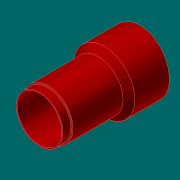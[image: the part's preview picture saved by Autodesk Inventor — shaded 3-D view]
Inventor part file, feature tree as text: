
AUTODESK INVENTOR PART (.ipt)
format: ipt  version: 2017.3 (Build 213256000, 256)  size: 176,128 bytes
history: native  units: in
note: dims shown in document units (in); Inventor stores cm internally (conversion verified against a paired STEP export)
features: extrude x4, sketch x3, chamfer x1, fillet x1
ambient origin geometry x8: Origin, YZ Plane, XZ Plane, XY Plane, X Axis, Y Axis, Z Axis, Center Point
bodies: Solid1 (feature_tree)
feature tree (9):
  sketch  "Sketch1"  dims[d0=2.875in d1=2.5984in]
  extrude  "Extrusion1"  Depth=2.5984in
  extrude  "Extrusion4"  Depth=21.25in
  chamfer  "Chamfer1"  Distance=0.5in
  extrude  "Extrusion2"  Depth=0.0312in TaperAngle=0.0deg
  extrude  "Extrusion3"  Depth=0.0312in
  fillet  "Fillet1"  Radius=3.5625in
  sketch  "Sketch2"  dims[d2=21.25in d3=0.0in d4=2.703in d5=0.5in d6=0.0in]
  sketch  "Sketch3"  dims[d7=31.0in d8=0.5in d9=0.0in d10=0.0312in d11=3.5625in d12=17.5in d13=0.0in d14=0.3438in d15=0.125in d16=45.0deg]
